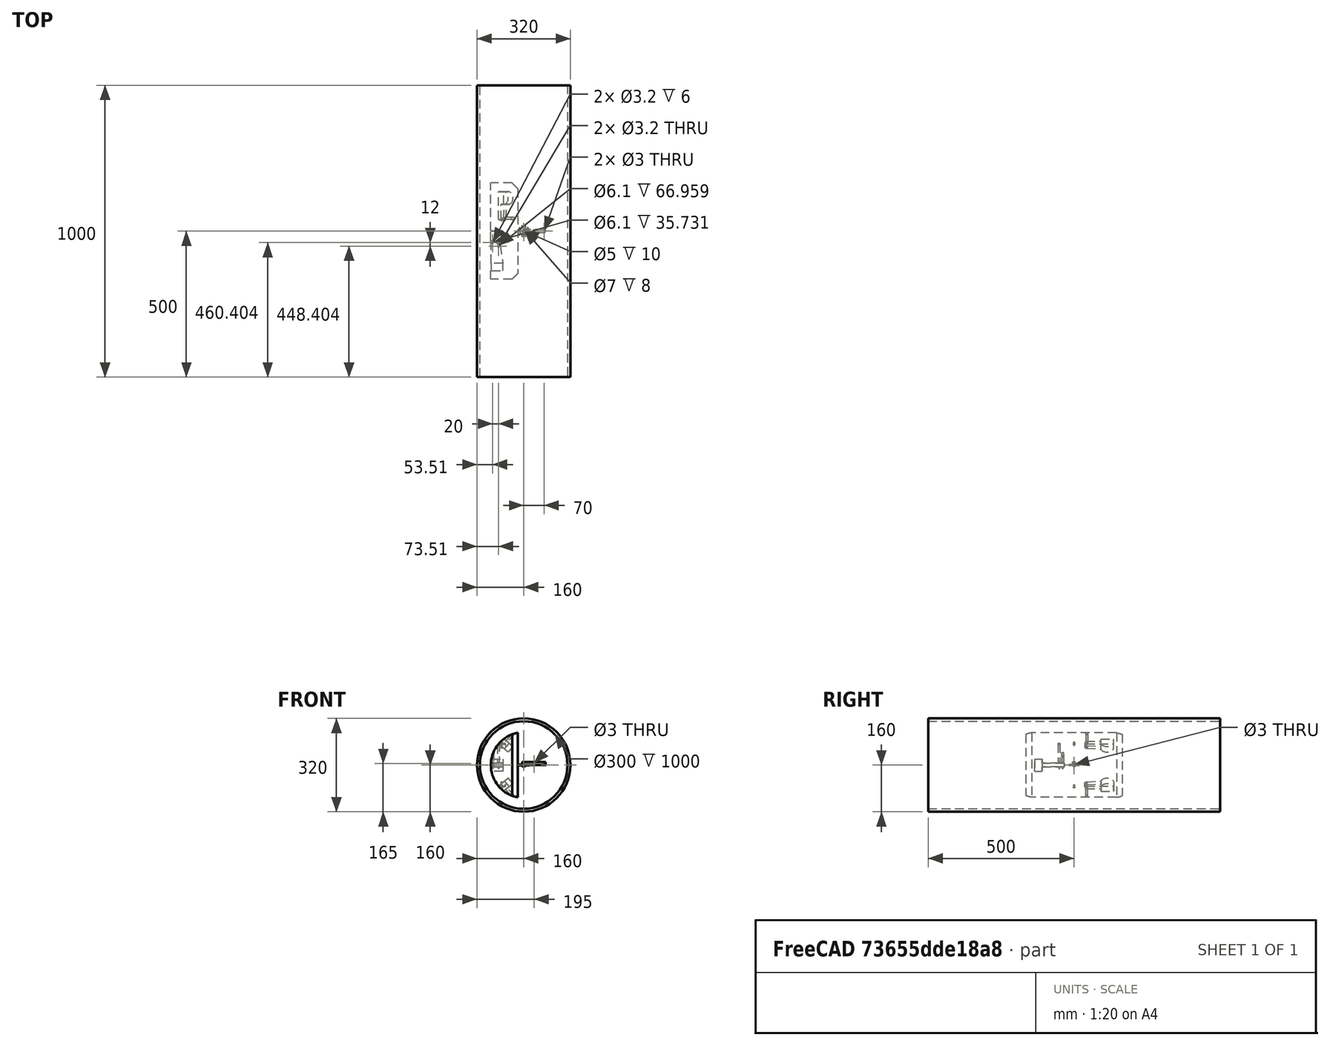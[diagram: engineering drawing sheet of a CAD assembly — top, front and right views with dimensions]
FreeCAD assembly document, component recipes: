
FREECAD ASSEMBLY — COMPONENT RECIPES ("Prototype_V1")

This assembly document has 6 components, labeled P0..P5 below (a component is one placed body or linked part). 4 of them carry a construction recipe — the FreeCAD feature program that regenerates the part from scratch, quoted from this document or its linked companion documents; the rest are supplied as boundary geometry only. No exploded tour is included for this assembly.
COMPONENT P0 — recipe-attached ("Pipe", modeled in this document).
Construction recipe (the document's own serialized feature program — sketch geometry with constraints, then the solid features built on it; lengths are millimeters unless a unit is written):

FEATURE [Sketcher::SketchObject] Sketch007
  ArcFitTolerance = 1e-06
  AttachmentSupport = -> [XZ_Plane001]
  ExternalBSplineMaxDegree = 5
  ExternalBSplineTolerance = 0.0001
  FullyConstrained = true
  InternalTolerance = 1e-06
  InvalidShape = false
  MakeInternals = true
  MapMode = 5
  Placement = pos=(0,0,0) rot=(1,0,0;1.5708rad)
  Support = -> [XZ_Plane001]
  TreeRank = 40
  ValidateShape = true
  expr: Constraints[1] = <<V>>.d_pipe
  sketch-geometry (1):
    g0: Circle CenterX=0 CenterY=0 CenterZ=0 NormalX=0 NormalY=0 NormalZ=1 AngleXU=0 Radius=150
  constraints (2):
    c: Coincident(g0,g-1)
    c: Diameter(g0) = 300
FEATURE [PartDesign::Pad] Pad001
  AddSubType = 0
  AlongSketchNormal = false
  AutoTaperInnerAngle = true
  CheckUpToFaceLimits = true
  ClaimChildren = false
  Direction = (0,-1,2e-16)
  Fit = 0
  FitJoin = 0
  InnerFit = 0
  InnerFitJoin = 0
  InvalidShape = false
  Length = 1000
  Length2 = 100
  Linearize = true
  Midplane = true
  NewSolid = false
  Profile = -> Sketch007
  Refine = true
  Suppress = false
  TaperInnerAngle = 0
  TaperInnerAngleRev = 0
  TreeRank = 41
  Type = 0
  ValidateShape = true
  _ProfileBasedVersion = 1
FEATURE [PartDesign::Thickness] Thickness
  AddSubType = 0
  Base = -> Pad001 [Face3,Face2]
  BaseFeature = -> Pad001
  Intersection = false
  InvalidShape = false
  Join = 0
  Mode = 0
  NewSolid = false
  Refine = true
  SupportTransform = false
  Suppress = false
  TreeRank = 42
  ValidateShape = true
  Value = 10
FEATURE [PartDesign::Body] Body001  label="Pipe"
  AutoGroupSolids = false
  ClaimAllChildren = false
  ExportMode = 0
  Group = -> [Sketch007,Pad001,Thickness]
  InvalidShape = false
  Origin = -> Origin001
  Tip = -> Thickness
  TreeRank = 39
  ValidateShape = true
  _ExportChildren = -> [Pad001,Thickness]
  _GroupVersion = 1
COMPONENT P1 — recipe-attached ("Link(Basic Link)", modeled in this document).
Construction recipe (the document's own serialized feature program — sketch geometry with constraints, then the solid features built on it; lengths are millimeters unless a unit is written):

FEATURE [Sketcher::SketchObject] Sketch008
  ArcFitTolerance = 1e-06
  AttachmentSupport = -> [XY_Plane002]
  ExternalBSplineMaxDegree = 5
  ExternalBSplineTolerance = 0.0001
  FullyConstrained = true
  InternalTolerance = 1e-06
  InvalidShape = false
  MakeInternals = true
  MapMode = 5
  Support = -> [XY_Plane002]
  TreeRank = 53
  ValidateShape = true
  sketch-geometry (6):
    g0: ArcOfCircle CenterX=0 CenterY=0 CenterZ=0 NormalX=0 NormalY=0 NormalZ=1 AngleXU=0 Radius=5 StartAngle=1.5708 EndAngle=4.71239
    g1: ArcOfCircle CenterX=70 CenterY=0 CenterZ=0 NormalX=0 NormalY=0 NormalZ=1 AngleXU=0 Radius=5 StartAngle=4.71239 EndAngle=7.85398
    g2: LineSegment StartX=-9e-16 StartY=-5 StartZ=0 EndX=70 EndY=-5 EndZ=0
    g3: LineSegment StartX=70 StartY=5 StartZ=0 EndX=0 EndY=5 EndZ=0
    g4: Circle CenterX=0 CenterY=0 CenterZ=0 NormalX=0 NormalY=0 NormalZ=1 AngleXU=0 Radius=1.5
    g5: Circle CenterX=70 CenterY=0 CenterZ=0 NormalX=0 NormalY=0 NormalZ=1 AngleXU=0 Radius=1.5
  constraints (13):
    c: Tangent(g0,g2) = -1.5708
    c: Tangent(g2,g1) = -1.5708
    c: Tangent(g1,g3) = -1.5708
    c: Tangent(g3,g0) = -1.5708
    c: Equal(g0,g1)
    c: Coincident(g0,g-1)
    c: PointOnObject(g1,g-1)
    c: Distance(g3) = 70
    c: Radius(g1) = 5
    c: Coincident(g4,g0)
    c: Coincident(g5,g1)
    c: Equal(g5,g4)
    c: Diameter(g4) = 3
FEATURE [PartDesign::Pad] Pad002
  AddSubType = 0
  AlongSketchNormal = false
  AutoTaperInnerAngle = true
  CheckUpToFaceLimits = true
  ClaimChildren = false
  Direction = (0,0,1)
  Fit = 0
  FitJoin = 0
  InnerFit = 0
  InnerFitJoin = 0
  InvalidShape = false
  Length = 10
  Length2 = 100
  Linearize = true
  NewSolid = false
  Profile = -> Sketch008
  Refine = true
  Suppress = false
  TaperInnerAngle = 0
  TaperInnerAngleRev = 0
  TreeRank = 54
  Type = 0
  ValidateShape = true
  _ProfileBasedVersion = 1
FEATURE [PartDesign::Pocket] Pocket007
  AddSubType = 1
  AutoTaperInnerAngle = true
  BaseFeature = -> Pad002
  CheckUpToFaceLimits = true
  ClaimChildren = false
  Fit = 2
  FitJoin = 0
  InnerFit = 0
  InnerFitJoin = 0
  InvalidShape = false
  Length = 8
  Length2 = 100
  Linearize = true
  NewSolid = false
  Profile = -> Pad002 [Edge15]
  Refine = true
  Suppress = false
  TaperInnerAngle = 0
  TaperInnerAngleRev = 0
  TreeRank = 87
  Type = 0
  ValidateShape = true
  _ProfileBasedVersion = 1
  _Version = 1
FEATURE [Sketcher::SketchObject] Sketch013
  ArcFitTolerance = 1e-06
  AttachmentSupport = -> [Pocket007]
  ExternalBSplineMaxDegree = 5
  ExternalBSplineTolerance = 0.0001
  ExternalGeometry = -> [Pocket007]
  FullyConstrained = true
  InternalTolerance = 1e-06
  InvalidShape = false
  MakeInternals = true
  MapMode = 5
  Placement = pos=(0,5,0) rot=(0,0.707107,0.707107;3.14159rad)
  Support = -> [Pocket007]
  TreeRank = 88
  ValidateShape = true
  sketch-geometry (1):
    g0: Circle CenterX=-35 CenterY=5 CenterZ=0 NormalX=0 NormalY=0 NormalZ=1 AngleXU=0 Radius=1.5
  constraints (2):
    c: Diameter(g0) = 3
    c: Symmetric(g-3,g-1,g0)
FEATURE [PartDesign::Pocket] Pocket008
  AddSubType = 1
  AutoTaperInnerAngle = true
  BaseFeature = -> Pocket007
  CheckUpToFaceLimits = true
  ClaimChildren = false
  Fit = 0
  FitJoin = 0
  InnerFit = 0
  InnerFitJoin = 0
  InvalidShape = false
  Length = 5
  Length2 = 100
  Linearize = true
  NewSolid = false
  Profile = -> Sketch013
  Refine = true
  Suppress = false
  TaperInnerAngle = 0
  TaperInnerAngleRev = 0
  TreeRank = 89
  Type = 1
  ValidateShape = true
  _ProfileBasedVersion = 1
  _Version = 1
FEATURE [PartDesign::Body] Body002  label="Basic Link"
  AutoGroupSolids = false
  ClaimAllChildren = false
  ExportMode = 0
  Group = -> [Sketch008,Pad002,Pocket007,Sketch013,Pocket008]
  InvalidShape = false
  Origin = -> Origin002
  Tip = -> Pocket008
  TreeRank = 175
  ValidateShape = true
  _ExportChildren = -> [Pad002,Pocket007,Pocket008]
  _GroupVersion = 1
COMPONENT P2 — recipe-attached ("Link001(Wheel)", modeled in this document).
Construction recipe (the document's own serialized feature program — sketch geometry with constraints, then the solid features built on it; lengths are millimeters unless a unit is written):

FEATURE [Sketcher::SketchObject] Sketch009
  ArcFitTolerance = 1e-06
  AttachmentSupport = -> [XY_Plane003]
  ExternalBSplineMaxDegree = 5
  ExternalBSplineTolerance = 0.0001
  FullyConstrained = true
  InternalTolerance = 1e-06
  InvalidShape = false
  MakeInternals = true
  MapMode = 5
  Support = -> [XY_Plane003]
  TreeRank = 65
  ValidateShape = true
  sketch-geometry (2):
    g0: Circle CenterX=0 CenterY=0 CenterZ=0 NormalX=0 NormalY=0 NormalZ=1 AngleXU=0 Radius=19
    g1: Circle CenterX=0 CenterY=0 CenterZ=0 NormalX=0 NormalY=0 NormalZ=1 AngleXU=0 Radius=2.5
  constraints (4):
    c: Diameter(g0) = 38
    c: Coincident(g0,g-1)
    c: Coincident(g1,g0)
    c: Diameter(g1) = 5
FEATURE [PartDesign::Pad] Pad003
  AddSubType = 0
  AlongSketchNormal = false
  AutoTaperInnerAngle = true
  CheckUpToFaceLimits = true
  ClaimChildren = false
  Direction = (0,0,1)
  Fit = 0
  FitJoin = 0
  InnerFit = 0
  InnerFitJoin = 0
  InvalidShape = false
  Length = 3
  Length2 = 100
  Linearize = true
  Midplane = true
  NewSolid = false
  Profile = -> Sketch009
  Refine = true
  Suppress = false
  TaperInnerAngle = 0
  TaperInnerAngleRev = 0
  TreeRank = 66
  Type = 0
  ValidateShape = true
  _ProfileBasedVersion = 1
FEATURE [Sketcher::SketchObject] Sketch010
  ArcFitTolerance = 1e-06
  AttachmentSupport = -> [XY_Plane003]
  ExternalBSplineMaxDegree = 5
  ExternalBSplineTolerance = 0.0001
  FullyConstrained = true
  InternalTolerance = 1e-06
  InvalidShape = false
  MakeInternals = true
  MapMode = 5
  Support = -> [XY_Plane003]
  TreeRank = 67
  ValidateShape = true
  sketch-geometry (4):
    g0: LineSegment StartX=3.5 StartY=12 StartZ=0 EndX=-3.5 EndY=12 EndZ=0
    g1: LineSegment StartX=-3.5 StartY=12 StartZ=0 EndX=-3.5 EndY=22 EndZ=0
    g2: LineSegment StartX=-3.5 StartY=22 StartZ=0 EndX=3.5 EndY=22 EndZ=0
    g3: LineSegment StartX=3.5 StartY=22 StartZ=0 EndX=3.5 EndY=12 EndZ=0
  constraints (11):
    c: Coincident(g0,g1)
    c: Coincident(g1,g2)
    c: Coincident(g2,g3)
    c: Coincident(g3,g0)
    c: Horizontal(g2)
    c: Vertical(g1)
    c: Vertical(g3)
    c: Distance(g0) = 7
    c: Symmetric(g0,g0,g-2)
    c: Distance(g3) = 10
    c: DistanceY(g0) = 12
FEATURE [PartDesign::Pocket] Pocket004
  AddSubType = 1
  AutoTaperInnerAngle = true
  BaseFeature = -> Pad003
  CheckUpToFaceLimits = true
  ClaimChildren = false
  Fit = 0
  FitJoin = 0
  InnerFit = 0
  InnerFitJoin = 0
  InvalidShape = false
  Length = 5
  Length2 = 100
  Linearize = true
  Midplane = true
  NewSolid = false
  Profile = -> Sketch010
  Refine = true
  Suppress = false
  TaperInnerAngle = 0
  TaperInnerAngleRev = 0
  TreeRank = 68
  Type = 1
  ValidateShape = true
  _ProfileBasedVersion = 1
  _Version = 1
FEATURE [PartDesign::PolarPattern] PolarPattern
  AddSubType = 0
  Angle = 360
  Axis = -> Sketch010 [N_Axis]
  BaseFeature = -> Pocket004
  CopyShape = false
  InvalidShape = false
  NewSolid = false
  Occurrences = 10
  OriginalSubs = -> [Pocket004]
  Originals = -> [Pocket004]
  ParallelTransform = true
  Refine = true
  SubTransform = true
  Suppress = false
  TreeRank = 69
  ValidateShape = true
  _Version = 3
FEATURE [PartDesign::Line] DatumLine
  AttacherType = Attacher::AttachEngineLine
  AttachmentOffset = pos=(1,0,0) rot=(0,0,1;0rad)
  AttachmentSupport = -> [PolarPattern]
  InvalidShape = false
  Length = 10
  MapMode = 42
  MinimumLength = 10
  Placement = pos=(0,16.3374,0) rot=(0.57735,0.57735,0.57735;2.0944rad)
  ResizeMode = 0
  Support = -> [PolarPattern]
  TreeRank = 70
  ValidateShape = true
FEATURE [Sketcher::SketchObject] Sketch011
  ArcFitTolerance = 1e-06
  AttachmentSupport = -> [XY_Plane003]
  ExternalBSplineMaxDegree = 5
  ExternalBSplineTolerance = 0.0001
  ExternalGeometry = -> [DatumLine]
  FullyConstrained = true
  InternalTolerance = 1e-06
  InvalidShape = false
  MakeInternals = true
  MapMode = 5
  Support = -> [XY_Plane003]
  TreeRank = 71
  ValidateShape = true
  sketch-geometry (4):
    g0: ArcOfCircle CenterX=0 CenterY=0 CenterZ=0 NormalX=0 NormalY=0 NormalZ=1 AngleXU=0 Radius=20 StartAngle=1.39743 EndAngle=1.74416
    g1: LineSegment StartX=-3.45 StartY=16.3374 StartZ=0 EndX=3.45 EndY=16.3374 EndZ=0
    g2: LineSegment StartX=3.45 StartY=16.3374 StartZ=0 EndX=3.45 EndY=19.7002 EndZ=0
    g3: LineSegment StartX=-3.45 StartY=19.7002 StartZ=0 EndX=-3.45 EndY=16.3374 EndZ=0
  constraints (11):
    c: Coincident(g1,g2)
    c: Coincident(g3,g1)
    c: Vertical(g2)
    c: Vertical(g3)
    c: PointOnObject(g1,g-3)
    c: Coincident(g0,g2)
    c: Coincident(g0,g3)
    c: Symmetric(g1,g1,g-2)
    c: Distance(g1) = 6.9
    c: Coincident(g-1,g0)
    c: Radius(g0) = 20
FEATURE [PartDesign::Revolution] Revolution
  AddSubType = 0
  Angle = 360
  Axis = (1,0,0)
  Base = (0,16.3374,0)
  ClaimChildren = false
  Fit = 0
  FitJoin = 0
  InnerFit = 0
  InnerFitJoin = 0
  InvalidShape = false
  Linearize = true
  NewSolid = true
  Profile = -> Sketch011
  ReferenceAxis = -> DatumLine
  Refine = true
  Reversed = true
  Suppress = false
  TreeRank = 72
  ValidateShape = true
  _ProfileBasedVersion = 1
FEATURE [PartDesign::Chamfer] Chamfer001
  AddSubType = 0
  Angle = 45
  Base = -> Revolution [Edge3,Edge1]
  BaseFeature = -> Revolution
  ChamferType = 0
  FlipDirection = false
  InvalidShape = false
  NewSolid = false
  Refine = true
  Size = 0.5
  Size2 = 1
  SupportTransform = false
  Suppress = false
  TreeRank = 74
  ValidateShape = true
FEATURE [PartDesign::PolarPattern] PolarPattern001
  AddSubType = 0
  Angle = 360
  Axis = -> Z_Axis003
  BaseFeature = -> Chamfer001
  CopyShape = false
  InvalidShape = false
  NewSolid = false
  Occurrences = 10
  OriginalSubs = -> [Revolution,Chamfer001]
  Originals = -> [Revolution,Chamfer001]
  ParallelTransform = true
  Refine = true
  SubTransform = true
  Suppress = false
  TreeRank = 73
  ValidateShape = true
  _Version = 3
FEATURE [PartDesign::Pad] Pad004
  AddSubType = 0
  AlongSketchNormal = false
  AutoTaperInnerAngle = true
  BaseFeature = -> PolarPattern
  CheckUpToFaceLimits = true
  ClaimChildren = false
  Direction = (0,0,1)
  Fit = 2
  FitJoin = 0
  InnerFit = 0
  InnerFitJoin = 0
  InvalidShape = false
  Length = 10
  Length2 = 100
  Linearize = true
  Midplane = true
  NewSolid = false
  Profile = -> Sketch009 [InternalFace2]
  Refine = true
  Suppress = false
  TaperInnerAngle = 0
  TaperInnerAngleRev = 0
  TreeRank = 75
  Type = 0
  ValidateShape = true
  _ProfileBasedVersion = 1
FEATURE [PartDesign::Pocket] Pocket005
  AddSubType = 1
  AutoTaperInnerAngle = true
  BaseFeature = -> Pad004
  CheckUpToFaceLimits = true
  ClaimChildren = false
  Fit = 0
  FitJoin = 0
  InnerFit = 0
  InnerFitJoin = 0
  InvalidShape = false
  Length = 5
  Length2 = 100
  Linearize = true
  Midplane = true
  NewSolid = false
  Profile = -> Sketch009 [InternalFace2]
  Refine = true
  Suppress = false
  TaperInnerAngle = 0
  TaperInnerAngleRev = 0
  TreeRank = 76
  Type = 1
  ValidateShape = true
  _ProfileBasedVersion = 1
  _Version = 1
FEATURE [PartDesign::Chamfer] Chamfer002
  AddSubType = 0
  Angle = 45
  Base = -> Pocket005 [Edge129,Edge126,Edge42,Edge124]
  BaseFeature = -> Pocket005
  ChamferType = 0
  FlipDirection = false
  InvalidShape = false
  NewSolid = false
  Refine = true
  Size = 1
  Size2 = 1
  SupportTransform = false
  Suppress = false
  TreeRank = 77
  ValidateShape = true
FEATURE [Part::SubShapeBinder] Import  label="Import(Hole001)"
  BindCopyOnChange = 0
  BindMode = 0
  ClaimChildren = false
  Context = -> Body003 [Import.]
  EdgeTolerance = 1e-06
  FillStyle = 0
  Fuse = false
  InvalidShape = false
  MakeFace = false
  MergeEdges = true
  OffsetFill = false
  OffsetIntersection = false
  OffsetJoinType = 0
  OffsetOpenResult = false
  Outline = false
  PartialLoad = false
  Relative = true
  SplitEdges = false
  Support = -> [Body[Hole001.]]
  TightBound = false
  TreeRank = 81
  ValidateShape = true
  _Version = 8
FEATURE [PartDesign::Plane] DatumPlane
  AttachmentSupport = -> [Import]
  InvalidShape = false
  Length = 104.532
  MapMode = 13
  MinimumLength = 10
  MinimumWidth = 10
  Placement = pos=(-112.34,-84.5321,2) rot=(0.57735,-0.57735,-0.57735;2.0944rad)
  ResizeMode = 0
  Support = -> [Import]
  TreeRank = 80
  ValidateShape = true
  Width = 10
FEATURE [PartDesign::Body] Body003  label="OmniWheel"
  AutoGroupSolids = false
  ClaimAllChildren = false
  ExportMode = 0
  Group = -> [Sketch009,Pad003,Sketch010,Pocket004,PolarPattern,DatumLine,Sketch011,Pad004,Pocket005,Chamfer002,Revolution,Chamfer001,PolarPattern001,DatumPlane,Import]
  InvalidShape = false
  Origin = -> Origin003
  Tip = -> Chamfer002
  TreeRank = 97
  ValidateShape = true
  _ExportChildren = -> [Pad003,Pocket004,PolarPattern,DatumLine,Pad004,Pocket005,Chamfer002,Revolution,Chamfer001,PolarPattern001,DatumPlane,Import]
  _GroupVersion = 1
COMPONENT P3 — recipe-attached ("Link002(Halve)", modeled in this document).
Construction recipe (the document's own serialized feature program — sketch geometry with constraints, then the solid features built on it; lengths are millimeters unless a unit is written):

FEATURE [Sketcher::SketchObject] Sketch
  ArcFitTolerance = 1e-06
  AttachmentSupport = -> [XZ_Plane]
  ExternalBSplineMaxDegree = 5
  ExternalBSplineTolerance = 0.0001
  FullyConstrained = true
  InternalTolerance = 1e-06
  InvalidShape = false
  MakeInternals = true
  MapMode = 5
  Placement = pos=(0,0,0) rot=(1,0,0;1.5708rad)
  Support = -> [XZ_Plane]
  TreeRank = 11
  ValidateShape = true
  expr: Constraints[4] = -0.5 * <<V>>.gap_width
  expr: Constraints[5] = 0.75 * <<V>>.d_pipe * 0.5
  sketch-geometry (2):
    g0: ArcOfCircle CenterX=0 CenterY=0 CenterZ=0 NormalX=0 NormalY=0 NormalZ=1 AngleXU=0 Radius=112.5 StartAngle=1.74952 EndAngle=4.53366
    g1: LineSegment StartX=-20 StartY=110.708 StartZ=0 EndX=-20 EndY=-110.708 EndZ=0
  constraints (6):
    c: Coincident(g0,g-1)
    c: Coincident(g1,g0)
    c: Vertical(g1)
    c: Coincident(g0,g1)
    c: DistanceX(g-2,g0) = -20
    c: Radius(g0) = 112.5
FEATURE [PartDesign::Pad] Pad
  AddSubType = 0
  AlongSketchNormal = false
  AutoTaperInnerAngle = true
  CheckUpToFaceLimits = true
  ClaimChildren = false
  Direction = (0,-1,0)
  Fit = 0
  FitJoin = 0
  InnerFit = 0
  InnerFitJoin = 0
  InvalidShape = false
  Length = 330
  Length2 = 100
  Linearize = true
  Midplane = true
  NewSolid = false
  Profile = -> Sketch
  Refine = true
  Suppress = false
  TaperInnerAngle = 0
  TaperInnerAngleRev = 0
  TreeRank = 12
  Type = 0
  ValidateShape = true
  _ProfileBasedVersion = 1
  expr: Length = 1.1 * <<V>>.d_pipe
FEATURE [PartDesign::Chamfer] Chamfer
  AddSubType = 0
  Angle = 45
  Base = -> Pad [Edge6,Edge5]
  BaseFeature = -> Pad
  ChamferType = 0
  FlipDirection = false
  InvalidShape = false
  NewSolid = false
  Refine = true
  Size = 20
  Size2 = 1
  SupportTransform = false
  Suppress = false
  TreeRank = 13
  ValidateShape = true
FEATURE [Sketcher::SketchObject] Sketch001
  ArcFitTolerance = 1e-06
  AttachmentOffset = pos=(0,0,0) rot=(0,1,0;0.698132rad)
  AttachmentSupport = -> [XY_Plane]
  ExternalBSplineMaxDegree = 5
  ExternalBSplineTolerance = 0.0001
  ExternalGeometry = -> [Chamfer]
  FullyConstrained = true
  InternalTolerance = 1e-06
  InvalidShape = false
  MakeInternals = true
  MapMode = 5
  Placement = pos=(0,0,0) rot=(0,1,0;0.698132rad)
  Support = -> [XY_Plane]
  TreeRank = 15
  ValidateShape = true
  expr: Constraints[10] = <<V>>.arm_length
  expr: Constraints[13] = <<V>>.d_wheel / 2 + 2
  expr: Constraints[15] = <<V>>.a_extrusion / 2 + 10
  expr: Constraints[1] = <<V>>.a_extrusion / 2 + 2
  expr: Constraints[2] = <<V>>.d_wheel / 2 + 2
  expr: Constraints[3] = <<V>>.a_extrusion / 2 + 2
  sketch-geometry (7):
    g0: LineSegment StartX=-89.7212 StartY=42.6625 StartZ=0 EndX=-85.72 EndY=91.6427 EndZ=0
    g1: ArcOfCircle CenterX=-90.9986 CenterY=113 CenterZ=0 NormalX=0 NormalY=0 NormalZ=1 AngleXU=0 Radius=22 StartAngle=4.95469 EndAngle=7.85398
    g2: LineSegment StartX=-90.9986 StartY=135 StartZ=0 EndX=-112.999 EndY=135 EndZ=0
    g3: ArcOfCircle CenterX=-96.698 CenterY=43.2324 CenterZ=0 NormalX=0 NormalY=0 NormalZ=1 AngleXU=0 Radius=7 StartAngle=4.45059 EndAngle=6.20168
    g4: LineSegment StartX=-112.999 StartY=135 StartZ=0 EndX=-112.999 EndY=40.3532 EndZ=0
    g5: LineSegment StartX=-112.999 StartY=40.3532 StartZ=0 EndX=-98.5097 EndY=36.4709 EndZ=0
    g6: LineSegment StartX=-85.72 StartY=91.6427 StartZ=0 EndX=-112.999 EndY=91.6427 EndZ=0
  constraints (21):
    c: Coincident(g1,g0)
    c: Distance(g1,g0) = 7
    c: Radius(g1) = 22
    c: Radius(g3) = 7
    c: Coincident(g2,g4)
    c: Coincident(g4,g5)
    c: Coincident(g5,g3)
    c: Tangent(g5,g3,g3) = -1.5708
    c: Tangent(g0,g3) = -1.5708
    c: Tangent(g1,g2) = -1.5708
    c: Distance(g1,g3) = 70
    c: Vertical(g4)
    c: Horizontal(g2)
    c: Distance(g2) = 22
    c: Angle(g5,g-1) = 0.261799
    c: Distance(g5) = 15
    c: Coincident(g6,g0)
    c: PointOnObject(g6,g4)
    c: Horizontal(g6)
    c: DistanceX(g2,g-3) = 0.5
    c: DistanceY(g2,g-3) = 30
FEATURE [PartDesign::Pocket] Pocket
  AddSubType = 1
  AutoTaperInnerAngle = true
  BaseFeature = -> Chamfer
  CheckUpToFaceLimits = true
  ClaimChildren = false
  Fit = 0
  FitJoin = 0
  InnerFit = 0
  InnerFitJoin = 0
  InvalidShape = false
  Length = 12
  Length2 = 100
  Linearize = true
  NewSolid = false
  Profile = -> Sketch001 [InternalFace2]
  Refine = true
  Reversed = true
  Suppress = false
  TaperInnerAngle = 0
  TaperInnerAngleRev = 0
  TreeRank = 17
  Type = 0
  ValidateShape = true
  _ProfileBasedVersion = 1
  _Version = 1
  expr: Length = <<V>>.a_extrusion + 2
FEATURE [PartDesign::Pocket] Pocket001
  AddSubType = 1
  AutoTaperInnerAngle = true
  BaseFeature = -> Pocket
  CheckUpToFaceLimits = true
  ClaimChildren = false
  Fit = 0
  FitJoin = 0
  InnerFit = 0
  InnerFitJoin = 0
  InvalidShape = false
  Length = 25
  Length2 = 100
  Linearize = true
  NewSolid = false
  Profile = -> Sketch001 [InternalFace1]
  Refine = true
  Reversed = true
  Suppress = false
  TaperInnerAngle = 0
  TaperInnerAngleRev = 0
  TreeRank = 18
  Type = 0
  ValidateShape = true
  _ProfileBasedVersion = 1
  _Version = 1
  expr: Length = <<V>>.a_extrusion * 2.5
FEATURE [Sketcher::SketchObject] Sketch003
  ArcFitTolerance = 1e-06
  AttachmentOffset = pos=(0,0,100) rot=(0,0,1;0rad)
  AttachmentSupport = -> [Sketch001]
  ExternalBSplineMaxDegree = 5
  ExternalBSplineTolerance = 0.0001
  ExternalGeometry = -> [Sketch001]
  FullyConstrained = true
  InternalTolerance = 1e-06
  InvalidShape = false
  MakeInternals = true
  MapMode = 5
  Placement = pos=(64.2788,1.1e-15,76.6044) rot=(0,1,0;0.698132rad)
  Support = -> [Sketch001]
  TreeRank = 20
  ValidateShape = true
  sketch-geometry (1):
    g0: Circle CenterX=-96.698 CenterY=43.2324 CenterZ=0 NormalX=0 NormalY=0 NormalZ=1 AngleXU=0 Radius=1.5
  constraints (2):
    c: Coincident(g0,g-3)
    c: Diameter(g0) = 3
FEATURE [PartDesign::Hole] Hole
  AddSubType = 1
  BaseFeature = -> Pocket001
  ClaimChildren = false
  CustomThreadClearance = 0
  Depth = 105
  DepthType = 0
  Diameter = 3.2
  DrillForDepth = false
  DrillPoint = 1
  DrillPointAngle = 118
  Fit = 0
  FitJoin = 0
  HoleCutCountersinkAngle = 90
  HoleCutCustomValues = false
  HoleCutDepth = 85
  HoleCutDiameter = 7
  HoleCutType = 1
  InnerFit = 0
  InnerFitJoin = 0
  InvalidShape = false
  Linearize = true
  ModelThread = false
  NewSolid = false
  Profile = -> Sketch003 [Edge1]
  Refine = true
  Suppress = false
  Tapered = false
  TaperedAngle = 90
  ThreadClass = 0
  ThreadDepth = 105
  ThreadDepthType = 0
  ThreadDirection = 0
  ThreadFit = 1
  ThreadSize = 9
  ThreadType = 1
  Threaded = false
  TreeRank = 21
  UseCustomThreadClearance = false
  ValidateShape = true
  _ProfileBasedVersion = 1
  expr: HoleCutDepth = 95 - <<V>>.a_extrusion
FEATURE [PartDesign::Mirrored] Mirrored
  AddSubType = 0
  BaseFeature = -> Hole
  CopyShape = false
  InvalidShape = false
  MirrorPlane = -> XY_Plane
  NewSolid = false
  OriginalSubs = -> [Hole,Pocket001,Pocket]
  Originals = -> [Hole,Pocket001,Pocket]
  ParallelTransform = true
  Refine = true
  SubTransform = true
  Suppress = false
  TreeRank = 22
  ValidateShape = true
  _Version = 3
FEATURE [Sketcher::SketchObject] Sketch004
  ArcFitTolerance = 1e-06
  AttachmentSupport = -> [XY_Plane]
  ExternalBSplineMaxDegree = 5
  ExternalBSplineTolerance = 0.0001
  ExternalGeometry = -> [Mirrored]
  FullyConstrained = true
  InternalTolerance = 1e-06
  InvalidShape = false
  MakeInternals = true
  MapMode = 5
  Support = -> [XY_Plane]
  TreeRank = 23
  ValidateShape = true
  expr: Constraints[22] = <<V>>.a_extrusion * 0.5 + 1
  expr: Constraints[26] = 25
  sketch-geometry (10):
    g0: ArcOfCircle CenterX=-106.49 CenterY=-39.5962 CenterZ=0 NormalX=0 NormalY=0 NormalZ=1 AngleXU=0 Radius=6 StartAngle=1.03038 EndAngle=1.5708
    g1: ArcOfCircle CenterX=-86.4901 CenterY=-51.5962 CenterZ=0 NormalX=0 NormalY=0 NormalZ=1 AngleXU=0 Radius=6 StartAngle=0.15173 EndAngle=1.03038
    g2: LineSegment StartX=-103.403 StartY=-34.4513 StartZ=0 EndX=-83.4031 EndY=-46.4513 EndZ=0
    g3: LineSegment StartX=-71.4901 StartY=-110 StartZ=0 EndX=-113.49 EndY=-110 EndZ=0
    g4: LineSegment StartX=-113.49 StartY=-110 StartZ=0 EndX=-113.49 EndY=-135 EndZ=0
    g5: LineSegment StartX=-113.49 StartY=-135 StartZ=0 EndX=-71.4901 EndY=-135 EndZ=0
    g6: LineSegment StartX=-71.4901 StartY=-135 StartZ=0 EndX=-71.4901 EndY=-110 EndZ=0
    g7: LineSegment StartX=-106.49 StartY=-33.5962 StartZ=0 EndX=-113.49 EndY=-33.5962 EndZ=0
    g8: LineSegment StartX=-80.559 StartY=-50.6893 StartZ=0 EndX=-71.4901 EndY=-110 EndZ=0
    g9: LineSegment StartX=-113.49 StartY=-33.5962 StartZ=0 EndX=-113.49 EndY=-110 EndZ=0
  constraints (31):
    c: Equal(g1,g0)
    c: DistanceY(g1,g0) = 12
    c: DistanceX(g0,g1) = 20
    c: Coincident(g2,g0)
    c: Coincident(g2,g1)
    c: Coincident(g3,g4)
    c: Coincident(g4,g5)
    c: Coincident(g5,g6)
    c: Coincident(g6,g3)
    c: Horizontal(g3)
    c: Horizontal(g5)
    c: Vertical(g4)
    c: Vertical(g6)
    c: Distance(g5) = 42
    c: DistanceX(g-3,g4) = -1
    c: Coincident(g7,g0)
    c: Vertical(g7,g3)
    c: Horizontal(g7)
    c: Tangent(g7,g0,g0) = -1.5708
    c: Distance(g7) = 7
    c: Tangent(g2,g0,g0) = 1.5708
    c: Tangent(g1,g2,g1) = 1.5708
    c: Radius(g1) = 6
    c: Coincident(g8,g1)
    c: Distance(g8) = 60
    c: Tangent(g1,g8,g1) = 1.5708
    c: Distance(g6) = 25
    c: Coincident(g8,g3)
    c: Coincident(g9,g7)
    c: Coincident(g9,g3)
    c: Distance(g-4,g5) = 30
FEATURE [PartDesign::Pocket] Pocket002
  AddSubType = 1
  AutoTaperInnerAngle = true
  BaseFeature = -> Mirrored
  CheckUpToFaceLimits = true
  ClaimChildren = false
  Fit = 0
  FitJoin = 0
  InnerFit = 0
  InnerFitJoin = 0
  InvalidShape = false
  Length = 12
  Length2 = 100
  Linearize = true
  Midplane = true
  NewSolid = false
  Profile = -> Sketch004 [InternalFace1]
  Refine = true
  Suppress = false
  TaperInnerAngle = 0
  TaperInnerAngleRev = 0
  TreeRank = 24
  Type = 0
  ValidateShape = true
  _ProfileBasedVersion = 1
  _Version = 1
  expr: Length = <<V>>.a_extrusion + 2
FEATURE [Sketcher::SketchObject] Sketch005
  ArcFitTolerance = 1e-06
  AttachmentSupport = -> [XY_Plane]
  ExternalBSplineMaxDegree = 5
  ExternalBSplineTolerance = 0.0001
  FullyConstrained = false
  InternalTolerance = 1e-06
  InvalidShape = false
  MakeInternals = true
  MapMode = 5
  Support = -> [XY_Plane]
  TreeRank = 26
  ValidateShape = true
  sketch-geometry (12):
    g0: ArcOfCircle CenterX=50.4849 CenterY=-51.0132 CenterZ=0 NormalX=0 NormalY=0 NormalZ=1 AngleXU=0 Radius=5 StartAngle=3.59219 EndAngle=6.73378
    g1: ArcOfCircle CenterX=20 CenterY=12 CenterZ=0 NormalX=0 NormalY=0 NormalZ=1 AngleXU=0 Radius=5 StartAngle=0.450593 EndAngle=3.59219
    g2: LineSegment StartX=54.9859 StartY=-48.8357 StartZ=0 EndX=24.5009 EndY=14.1775 EndZ=0
    g3: LineSegment StartX=15.4991 StartY=9.8225 StartZ=0 EndX=45.984 EndY=-53.1907 EndZ=0
    g4: ArcOfCircle CenterX=30.4849 CenterY=-63.0132 CenterZ=0 NormalX=0 NormalY=0 NormalZ=1 AngleXU=0 Radius=5 StartAngle=3.59219 EndAngle=6.73378
    g5: ArcOfCircle CenterX=0 CenterY=0 CenterZ=0 NormalX=0 NormalY=0 NormalZ=1 AngleXU=0 Radius=5 StartAngle=0.450593 EndAngle=3.59219
    g6: LineSegment StartX=34.9859 StartY=-60.8357 StartZ=0 EndX=4.50095 EndY=2.1775 EndZ=0
    g7: LineSegment StartX=-4.50095 StartY=-2.1775 StartZ=0 EndX=25.984 EndY=-65.1907 EndZ=0
    g8: ArcOfCircle CenterX=41.492 CenterY=111.619 CenterZ=0 NormalX=0 NormalY=0 NormalZ=1 AngleXU=0 Radius=7.45731 StartAngle=4.67486 EndAngle=7.81645
    g9: ArcOfCircle CenterX=13.3276 CenterY=112.676 CenterZ=0 NormalX=0 NormalY=0 NormalZ=1 AngleXU=0 Radius=7.45731 StartAngle=1.53327 EndAngle=4.67486
    g10: LineSegment StartX=41.7718 StartY=119.071 StartZ=0 EndX=13.6074 EndY=120.128 EndZ=0
    g11: LineSegment StartX=13.0478 StartY=105.224 StartZ=0 EndX=41.2122 EndY=104.167 EndZ=0
  constraints (23):
    c: Tangent(g0,g2) = -1.5708
    c: Tangent(g2,g1) = -1.5708
    c: Tangent(g1,g3) = -1.5708
    c: Tangent(g3,g0) = -1.5708
    c: Equal(g0,g1)
    c: Radius(g0) = 5
    c: Distance(g3) = 70
    c: Tangent(g4,g6) = -1.5708
    c: Tangent(g6,g5) = -1.5708
    c: Tangent(g5,g7) = -1.5708
    c: Tangent(g7,g4) = -1.5708
    c: Equal(g4,g5)
    c: Radius(g4) = 5
    c: Parallel(g7,g2)
    c: Distance(g7) = 70
    c: DistanceX(g5,g1) = 20
    c: DistanceY(g5,g1) = 12
    c: Coincident(g5,g-1)
    c: Tangent(g8,g10) = -1.5708
    c: Tangent(g10,g9) = -1.5708
    c: Tangent(g9,g11) = -1.5708
    c: Tangent(g11,g8) = -1.5708
    c: Equal(g8,g9)
FEATURE [PartDesign::Pocket] Pocket003
  AddSubType = 1
  AutoTaperInnerAngle = true
  BaseFeature = -> Pocket002
  CheckUpToFaceLimits = true
  ClaimChildren = false
  Fit = 0
  FitJoin = 0
  InnerFit = 0
  InnerFitJoin = 0
  InvalidShape = false
  Length = 42
  Length2 = 100
  Linearize = true
  Midplane = true
  NewSolid = false
  Profile = -> Sketch004 [InternalFace2]
  Refine = true
  Suppress = false
  TaperInnerAngle = 0
  TaperInnerAngleRev = 0
  TreeRank = 27
  Type = 0
  ValidateShape = true
  _ProfileBasedVersion = 1
  _Version = 1
FEATURE [Sketcher::SketchObject] Sketch006
  ArcFitTolerance = 1e-06
  AttachmentOffset = pos=(0,0,100) rot=(0,0,1;0rad)
  AttachmentSupport = -> [Sketch004]
  ExternalBSplineMaxDegree = 5
  ExternalBSplineTolerance = 0.0001
  ExternalGeometry = -> [Sketch004]
  FullyConstrained = true
  InternalTolerance = 1e-06
  InvalidShape = false
  MakeInternals = true
  MapMode = 5
  Placement = pos=(0,0,100) rot=(0,0,1;0rad)
  Support = -> [Sketch004]
  TreeRank = 28
  ValidateShape = true
  sketch-geometry (2):
    g0: Circle CenterX=-106.49 CenterY=-39.5962 CenterZ=0 NormalX=0 NormalY=0 NormalZ=1 AngleXU=0 Radius=1.5
    g1: Circle CenterX=-86.4901 CenterY=-51.5962 CenterZ=0 NormalX=0 NormalY=0 NormalZ=1 AngleXU=0 Radius=1.5
  constraints (4):
    c: Coincident(g0,g-3)
    c: Coincident(g1,g-4)
    c: Equal(g1,g0)
    c: Diameter(g0) = 3
FEATURE [PartDesign::Hole] Hole001
  AddSubType = 1
  BaseFeature = -> Pocket003
  ClaimChildren = false
  CustomThreadClearance = 0
  Depth = 112
  DepthType = 0
  Diameter = 3.2
  DrillForDepth = false
  DrillPoint = 0
  DrillPointAngle = 118
  Fit = 0
  FitJoin = 0
  HoleCutCountersinkAngle = 90
  HoleCutCustomValues = false
  HoleCutDepth = 91.5
  HoleCutDiameter = 6.1
  HoleCutType = 1
  InnerFit = 0
  InnerFitJoin = 0
  InvalidShape = false
  Linearize = true
  ModelThread = false
  NewSolid = false
  Profile = -> Sketch006
  Refine = true
  Suppress = false
  Tapered = false
  TaperedAngle = 90
  ThreadClass = 0
  ThreadDepth = 112
  ThreadDepthType = 0
  ThreadDirection = 0
  ThreadFit = 1
  ThreadSize = 9
  ThreadType = 1
  Threaded = false
  TreeRank = 29
  UseCustomThreadClearance = false
  ValidateShape = true
  _ProfileBasedVersion = 1
FEATURE [Sketcher::SketchObject] Sketch012
  ArcFitTolerance = 1e-06
  AttachmentOffset = pos=(0,0,-200) rot=(0,0,1;0rad)
  AttachmentSupport = -> [YZ_Plane]
  ExternalBSplineMaxDegree = 5
  ExternalBSplineTolerance = 0.0001
  ExternalGeometry = -> [Hole001]
  FullyConstrained = true
  InternalTolerance = 1e-06
  InvalidShape = false
  MakeInternals = true
  MapMode = 5
  Placement = pos=(-200,4.44e-14,-4.44e-14) rot=(0.57735,0.57735,0.57735;2.0944rad)
  Support = -> [YZ_Plane]
  TreeRank = 82
  ValidateShape = true
  sketch-geometry (1):
    g0: Circle CenterX=0 CenterY=0 CenterZ=0 NormalX=0 NormalY=0 NormalZ=1 AngleXU=0 Radius=1.5
  constraints (2):
    c: Coincident(g0,g-1)
    c: Diameter(g0) = 3
FEATURE [PartDesign::Pocket] Pocket006
  AddSubType = 1
  AutoTaperInnerAngle = true
  BaseFeature = -> Hole001
  CheckUpToFaceLimits = false
  ClaimChildren = false
  Fit = 0
  FitJoin = 0
  InnerFit = 0
  InnerFitJoin = 0
  InvalidShape = false
  Length = 0
  Length2 = 100
  Linearize = true
  NewSolid = false
  Offset = 12
  Profile = -> Sketch012
  Refine = true
  Reversed = true
  Suppress = false
  TaperInnerAngle = 0
  TaperInnerAngleRev = 0
  TreeRank = 83
  Type = 3
  UpToFace = -> Hole001 [Face1]
  ValidateShape = true
  _ProfileBasedVersion = 1
  _Version = 1
FEATURE [PartDesign::Chamfer] Chamfer003
  AddSubType = 0
  Angle = 45
  Base = -> Pocket006 [Edge19]
  BaseFeature = -> Pocket006
  ChamferType = 0
  FlipDirection = false
  InvalidShape = false
  NewSolid = false
  Refine = true
  Size = 1
  Size2 = 1
  SupportTransform = false
  Suppress = false
  TreeRank = 84
  ValidateShape = true
FEATURE [PartDesign::PolarPattern] PolarPattern002
  AddSubType = 0
  Angle = 43
  Axis = -> Y_Axis
  BaseFeature = -> Chamfer003
  CopyShape = false
  InvalidShape = false
  NewSolid = false
  Occurrences = 2
  OriginalSubs = -> [Chamfer003,Pocket006]
  Originals = -> [Chamfer003,Pocket006]
  ParallelTransform = true
  Refine = true
  SubTransform = true
  Suppress = false
  TreeRank = 85
  ValidateShape = true
  _Version = 3
FEATURE [PartDesign::Mirrored] Mirrored001
  AddSubType = 0
  BaseFeature = -> PolarPattern002
  CopyShape = false
  InvalidShape = false
  MirrorPlane = -> XY_Plane
  NewSolid = false
  ParallelTransform = true
  Refine = true
  SubTransform = true
  Suppress = false
  TreeRank = 86
  ValidateShape = true
  _Version = 3
FEATURE [PartDesign::Body] Body  label="Main_body"
  AutoGroupSolids = false
  ClaimAllChildren = false
  ExportMode = 0
  Group = -> [Sketch,Pad,Chamfer,Sketch001,Pocket,Pocket001,Sketch003,Hole,Mirrored,Sketch004,Pocket002,Pocket003,Sketch006,Sketch005,Hole001,Sketch012,Pocket006,Chamfer003,PolarPattern002,Mirrored001]
  InvalidShape = false
  Origin = -> Origin
  Tip = -> Mirrored001
  TreeRank = 10
  ValidateShape = true
  _ExportChildren = -> [Pad,Chamfer,Pocket,Pocket001,Hole,Mirrored,Pocket002,Pocket003,Sketch005,Hole001,Pocket006,Chamfer003,PolarPattern002,Mirrored001]
  _GroupVersion = 1
COMPONENT P4 — geometry summary ("Link004(*Wheel)"; no construction recipe available for this part):
  bounding box: 38.0 x 37.3 x 10.0 mm
  tessellated surface: 2,784 triangles
  volume: 2208 mm^3 (16% of its bounding box)
  symmetry: 2-fold rotationally symmetric about the x axis; 2-fold rotationally symmetric about the y axis; 2-fold rotationally symmetric about the z axis; mirror-symmetric across its x mid-plane, y mid-plane, z mid-plane
COMPONENT P5 — geometry summary ("Link007(*Basic Link)"; no construction recipe available for this part):
  bounding box: 67.2 x 50.4 x 10.0 mm
  tessellated surface: 912 triangles
  volume: 7322 mm^3 (22% of its bounding box)
PROVENANCE & LICENSES
A FreeCAD (.FCStd) document from a public repository crawl; recipes are the document's own serialized feature recipes (and, for linked parts, companion documents' recipes).
License: as declared in the source repository (recorded in the dataset sidecar).
